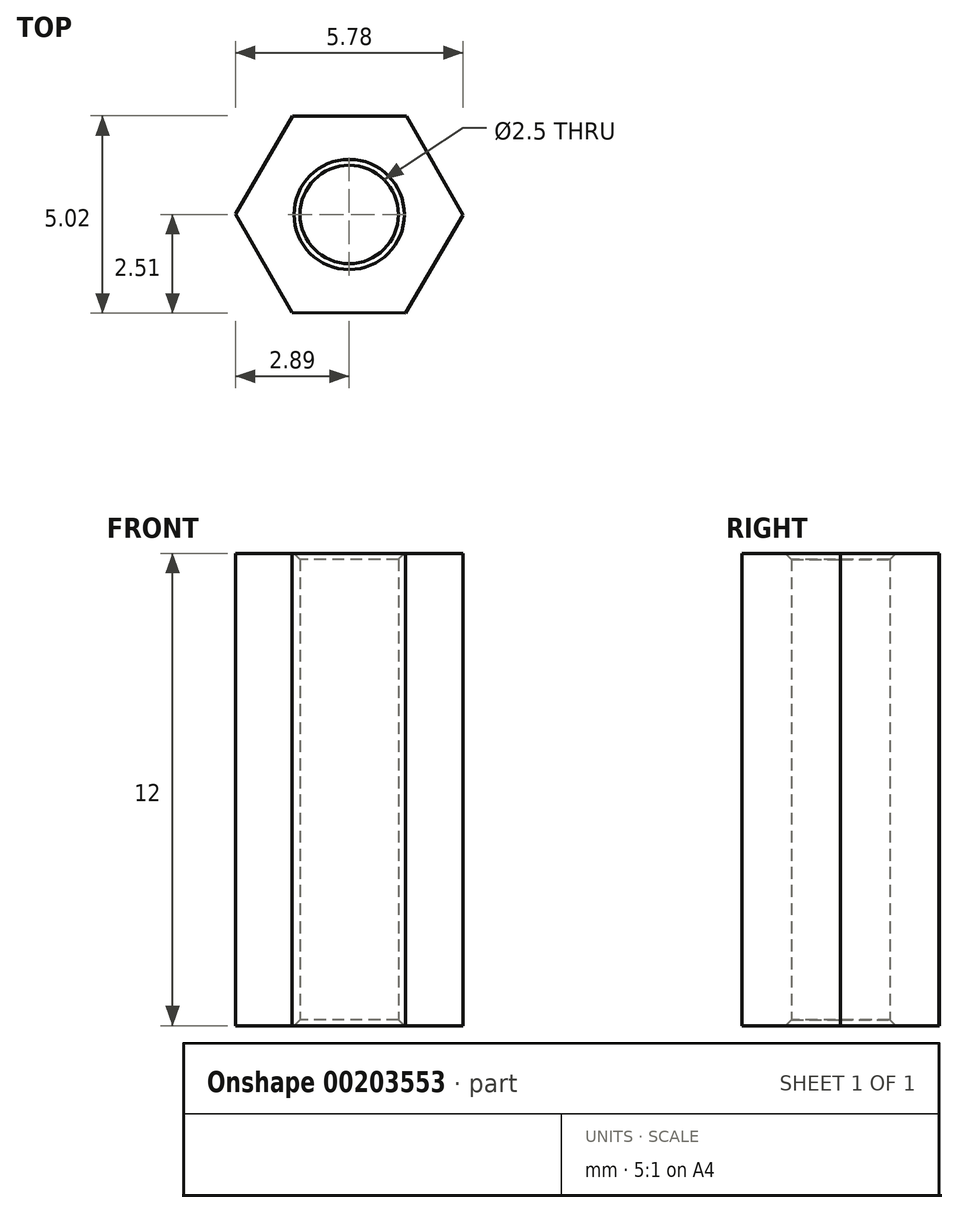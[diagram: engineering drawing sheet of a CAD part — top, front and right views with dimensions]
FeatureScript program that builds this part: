
annotation { "Feature Type Name" : "Feature", "Feature Type Description" : "" }
export const myFeature = defineFeature(function(context is Context, id is Id, definition is map)
    precondition{}
    {
        {
            var Q0;
            Q0=qCreatedBy(makeId("Top.planeOp"),FACE);
            var sketch = newSketch(context, id + "F0", { "sketchPlane" : qUnion([Q0])});
            skCircle(sketch, "E0.cCircle", {"center": v(0, 0) * mm, "radius": 2.5 * mm, "construction": true});
            skLineSegment(sketch, "E0.0", {"start": v(2.89, -0.01) * mm, "end": v(1.43, -2.5) * mm});
            skLineSegment(sketch, "E0.1", {"start": v(1.43, -2.5) * mm, "end": v(-1.45, -2.5) * mm});
            skLineSegment(sketch, "E0.2", {"start": v(-1.45, -2.5) * mm, "end": v(-2.89, 0.01) * mm});
            skLineSegment(sketch, "E0.3", {"start": v(-2.89, 0.01) * mm, "end": v(-1.43, 2.5) * mm});
            skLineSegment(sketch, "E0.4", {"start": v(-1.43, 2.5) * mm, "end": v(1.45, 2.5) * mm});
            skLineSegment(sketch, "E0.5", {"start": v(1.45, 2.5) * mm, "end": v(2.89, -0.01) * mm});
            skPoint(sketch, "E0.0.midPoint", {"position": v(2.16, -1.26) * mm});
            skCircle(sketch, "E1", {"center": v(0, 0) * mm, "radius": 1.25 * mm});
            skSolve(sketch);
        }
        {
            var Q0;
            Q0=makeQuery(id+"F0.imprint","IMPRINT",FACE,{"disambiguationData":[TD([[makeQuery(id+"F0.imprint","IMPRINT",EDGE,{"derivedFrom":sQuery(id+"F0.wireOp",EDGE,"E0.0")}),-1.0]])]});
            extrude(context, id + "F1", {"entities" : qUnion([Q0]), "depth" : 12 * mm});
        }
        {
            var Q0;
            Q0=qSketchRegion(id+"F0",true);
            extrude(context, id + "F2", {"entities" : qUnion([Q0]), "operationType" : NewBodyOperationType.REMOVE, "oppositeDirection" : true, "depth" : 12 * mm});
        }
        {
            var Q0;
            Q0=makeQuery(id+"F1.opExtrude","SWEPT_FACE",FACE,{"disambiguationData":[OSD([sQuery(id+"F0.wireOp",EDGE,"E1")])]});
            chamfer(context, id + "F3", {"entities" : qUnion([Q0]), "width" : 0.15 * mm, "tangentPropagation" : true});
        }
    });
